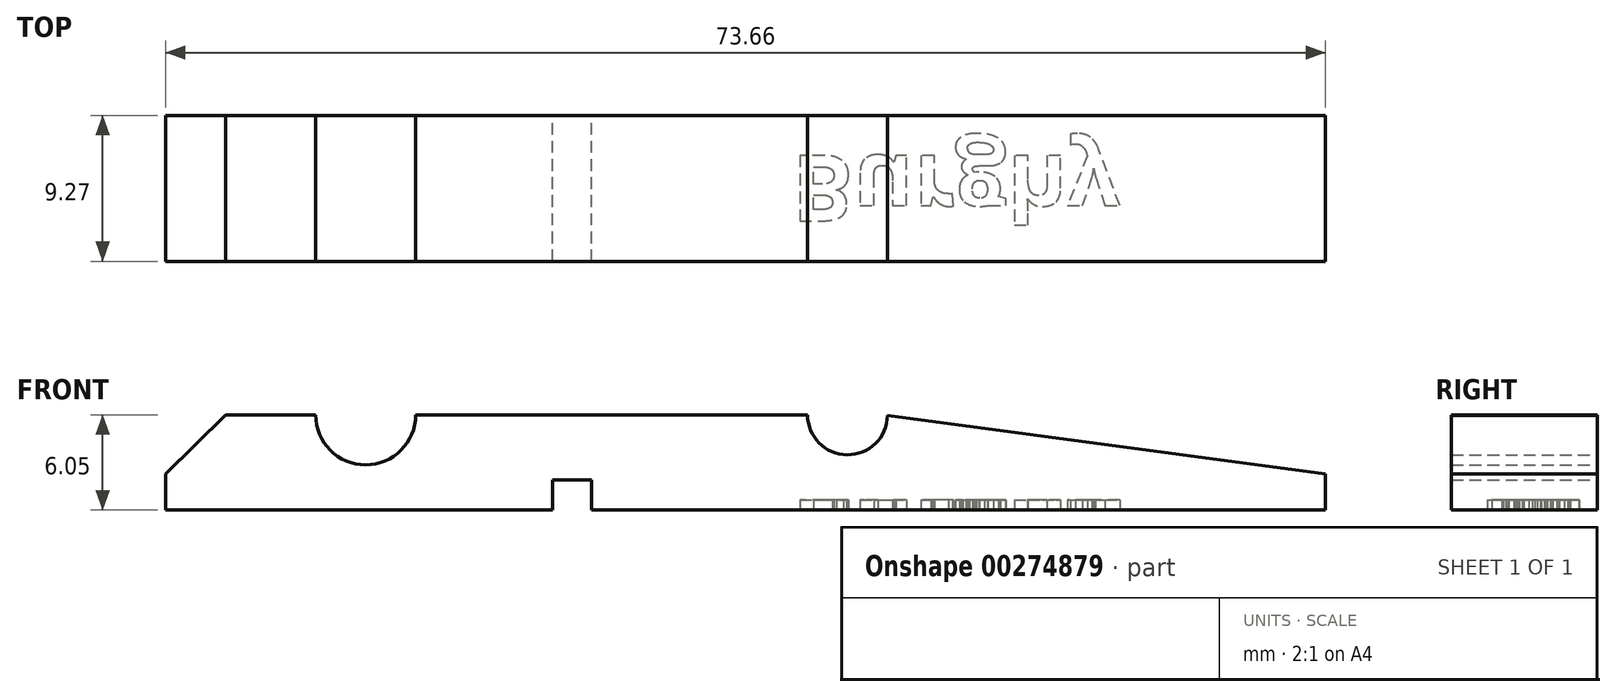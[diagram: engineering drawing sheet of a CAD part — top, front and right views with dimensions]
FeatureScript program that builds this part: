
annotation { "Feature Type Name" : "Feature", "Feature Type Description" : "" }
export const myFeature = defineFeature(function(context is Context, id is Id, definition is map)
    precondition{}
    {
        {
            var Q0;
            Q0=qCreatedBy(makeId("Front.planeOp"),FACE);
            var sketch = newSketch(context, id + "F0", { "sketchPlane" : qUnion([Q0])});
            skLineSegment(sketch, "E0.bottom", {"start": v(-10.9, -2.29) * mm, "end": v(13.66, -2.29) * mm});
            skLineSegment(sketch, "E0.left", {"start": v(-10.9, -2.29) * mm, "end": v(-10.9, 0) * mm});
            skLineSegment(sketch, "E0.right", {"start": v(62.76, -2.29) * mm, "end": v(62.76, 0) * mm});
            skLineSegment(sketch, "E1.top", {"start": v(-7.09, 3.76) * mm, "end": v(-1.37, 3.76) * mm});
            skLineSegment(sketch, "E2", {"start": v(-7.09, 3.76) * mm, "end": v(-10.9, 0) * mm});
            skLineSegment(sketch, "E3", {"start": v(34.95, 3.71) * mm, "end": v(62.76, 0) * mm});
            skArc(sketch, "E4", {"start": v(-1.37, 3.76) * mm, "mid": v(1.8, 0.58) * mm, "end": v(4.98, 3.76) * mm});
            skLineSegment(sketch, "E5.trimOffspring", {"start": v(4.98, 3.76) * mm, "end": v(29.87, 3.76) * mm});
            skPoint(sketch, "E6.center.orphan", {"position": v(32.4, 3.76) * mm});
            skArc(sketch, "E7", {"start": v(29.87, 3.76) * mm, "mid": v(32.38, 1.22) * mm, "end": v(34.95, 3.71) * mm});
            skLineSegment(sketch, "E8.top", {"start": v(13.66, -0.38) * mm, "end": v(16.15, -0.38) * mm});
            skLineSegment(sketch, "E8.left", {"start": v(13.66, -2.29) * mm, "end": v(13.66, -0.38) * mm});
            skLineSegment(sketch, "E8.right", {"start": v(16.15, -2.29) * mm, "end": v(16.15, -0.38) * mm});
            skLineSegment(sketch, "E9.trimOffspring", {"start": v(16.15, -2.29) * mm, "end": v(62.76, -2.29) * mm});
            skSolve(sketch);
        }
        {
            var Q0;
            Q0=makeQuery(id+"F0.imprint","IMPRINT",FACE,{"disambiguationData":[TD([[makeQuery(id+"F0.imprint","IMPRINT",EDGE,{"derivedFrom":sQuery(id+"F0.wireOp",EDGE,"E0.bottom")}),1.0]])]});
            extrude(context, id + "F1", {"entities" : qUnion([Q0]), "depth" : 9.27 * mm});
        }
        {
            var Q0;
            Q0=makeQuery(id+"F1.opExtrude","SWEPT_FACE",FACE,{"disambiguationData":[OSD([sQuery(id+"F0.wireOp",EDGE,"E9.trimOffspring")])]});
            var sketch = newSketch(context, id + "F2", { "sketchPlane" : qUnion([Q0])});
            skText(sketch, "E10", { "text": "Burghy", "fontName": "OpenSans-Bold.ttf"});
            const initialGuessF2  = {"E10": [0.02885, 0.00254, 1, 0, 0.0042]};
            skSetInitialGuess(sketch, initialGuessF2);
            skSolve(sketch);
        }
        {
            var Q0;
            Q0 = qSketchRegion(id + "F2", true);
            extrude(context, id + "F3", {"entities" : qUnion([Q0]), "operationType" : NewBodyOperationType.REMOVE, "oppositeDirection" : true, "depth" : 0.64 * mm});
        }
    });
